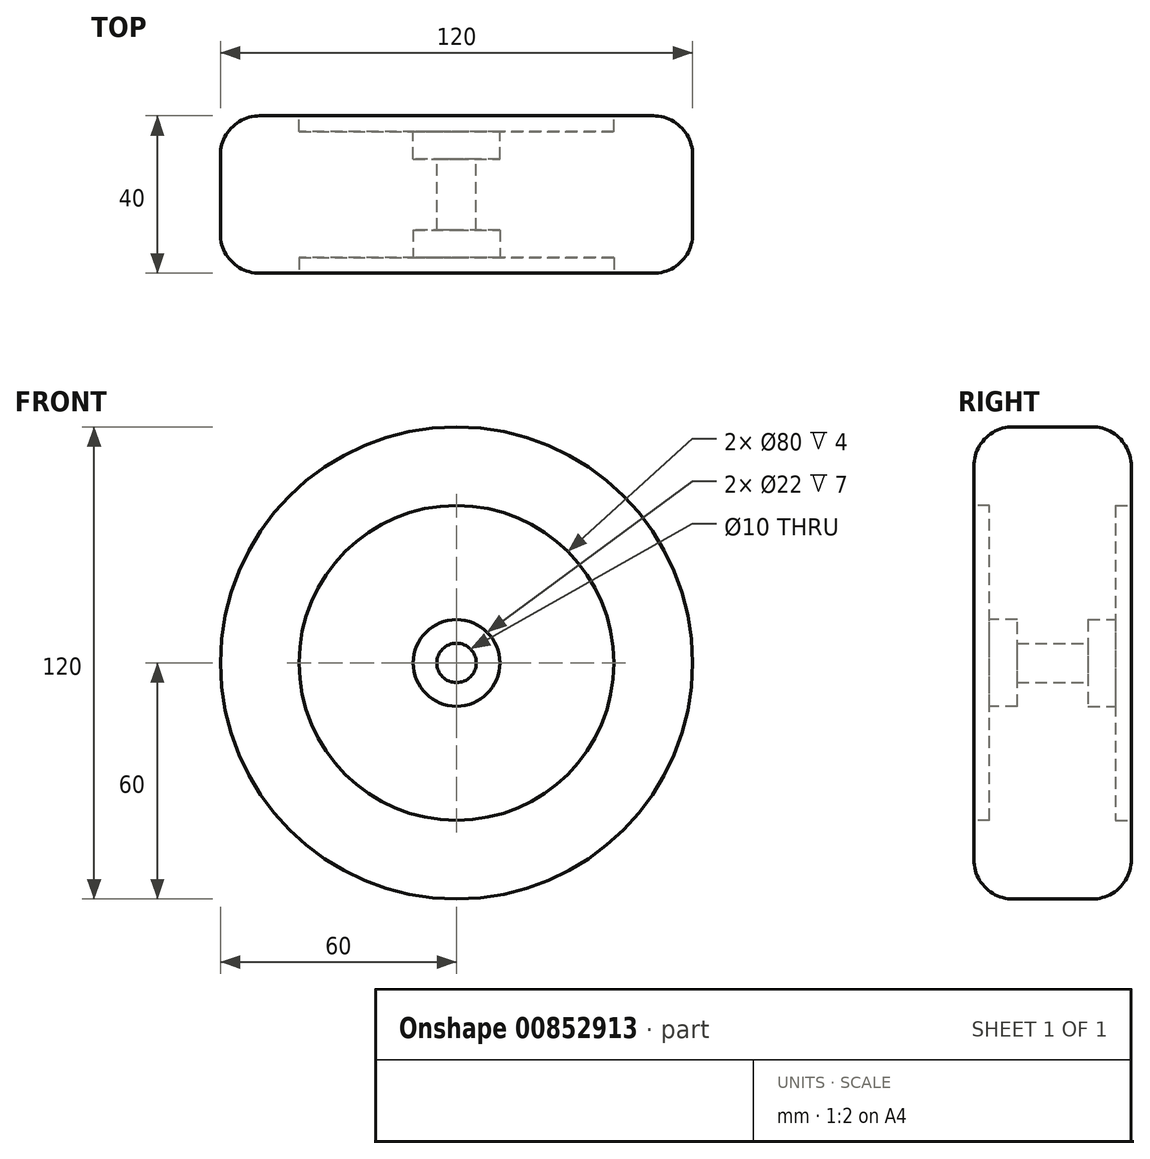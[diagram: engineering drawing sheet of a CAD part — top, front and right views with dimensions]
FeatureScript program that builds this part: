
annotation { "Feature Type Name" : "Feature", "Feature Type Description" : "" }
export const myFeature = defineFeature(function(context is Context, id is Id, definition is map)
    precondition{}
    {
        {
            var Q0;
            Q0=qCreatedBy(makeId("Front.planeOp"),FACE);
            var sketch = newSketch(context, id + "F0", { "sketchPlane" : qUnion([Q0])});
            skCircle(sketch, "E0", {"center": v(0, 0) * mm, "radius": 60 * mm});
            skSolve(sketch);
        }
        {
            var Q0;
            Q0=makeQuery(id+"F0.imprint","IMPRINT",FACE,{"disambiguationData":[TD([[makeQuery(id+"F0.imprint","IMPRINT",EDGE,{"derivedFrom":sQuery(id+"F0.wireOp",EDGE,"E0")}),1.0]])]});
            extrude(context, id + "F1", {"entities" : qUnion([Q0]), "depth" : 40 * mm, "offsetDistance" : 25 * mm});
        }
        {
            var Q0;
            Q0=makeQuery(id+"F1.opExtrude","CAP_FACE",FACE,{"disambiguationData":[OSD([sQuery(id+"F0.wireOp",EDGE,"E0")])],"isStart":false});
            var sketch = newSketch(context, id + "F2", { "sketchPlane" : qUnion([Q0])});
            skCircle(sketch, "E1", {"center": v(0, 0) * mm, "radius": 40 * mm});
            skSolve(sketch);
        }
        {
            var Q0;
            Q0=makeQuery(id+"F1.opExtrude","CAP_FACE",FACE,{"disambiguationData":[OSD([sQuery(id+"F0.wireOp",EDGE,"E0")])],"isStart":true});
            var Q1;
            Q1=makeQuery(id+"F1.opExtrude","SWEPT_FACE",FACE,{"disambiguationData":[OSD([sQuery(id+"F0.wireOp",EDGE,"E0")])]});
            fillet(context, id + "F3", {"entities" : qUnion([Q0, Q1]), "radius" : 10 * mm, "tangentPropagation" : true, "allowEdgeOverflow" : false});
        }
        {
            var Q0;
            Q0=makeQuery(id+"F2.imprint","IMPRINT",FACE,{"disambiguationData":[TD([[makeQuery(id+"F2.imprint","IMPRINT",EDGE,{"derivedFrom":sQuery(id+"F2.wireOp",EDGE,"E1")}),1.0]])]});
            extrude(context, id + "F4", {"entities" : qUnion([Q0]), "operationType" : NewBodyOperationType.REMOVE, "oppositeDirection" : true, "depth" : 4 * mm, "offsetDistance" : 25 * mm});
        }
        {
            var Q0;
            Q0=makeQuery(id+"F1.opExtrude","CAP_FACE",FACE,{"disambiguationData":[OSD([sQuery(id+"F0.wireOp",EDGE,"E0")])],"isStart":true});
            var sketch = newSketch(context, id + "F5", { "sketchPlane" : qUnion([Q0])});
            skCircle(sketch, "E2", {"center": v(0, 0) * mm, "radius": 40 * mm});
            skSolve(sketch);
        }
        {
            var Q0;
            Q0=makeQuery(id+"F5.imprint","IMPRINT",FACE,{"disambiguationData":[TD([[makeQuery(id+"F5.imprint","IMPRINT",EDGE,{"derivedFrom":sQuery(id+"F5.wireOp",EDGE,"E2")}),1.0]])]});
            extrude(context, id + "F6", {"entities" : qUnion([Q0]), "operationType" : NewBodyOperationType.REMOVE, "oppositeDirection" : true, "depth" : 4 * mm, "offsetDistance" : 25 * mm});
        }
        {
            var Q0;
            Q0=makeQuery(id+"F6.boolean.opBoolean","COPY",FACE,{"derivedFrom":makeQuery(id+"F6.opExtrude","CAP_FACE",FACE,{"disambiguationData":[OSD([sQuery(id+"F5.wireOp",EDGE,"E2")])],"isStart":false})});
            var sketch = newSketch(context, id + "F7", { "sketchPlane" : qUnion([Q0])});
            skCircle(sketch, "E3", {"center": v(0, 0) * mm, "radius": 11 * mm});
            skCircle(sketch, "E4", {"center": v(0, 0) * mm, "radius": 11.17 * mm});
            skSolve(sketch);
        }
        {
            var Q0;
            Q0=makeQuery(id+"F7.imprint","IMPRINT",FACE,{"disambiguationData":[TD([[makeQuery(id+"F7.imprint","IMPRINT",EDGE,{"derivedFrom":sQuery(id+"F7.wireOp",EDGE,"E3")}),1.0]])]});
            extrude(context, id + "F8", {"entities" : qUnion([Q0]), "operationType" : NewBodyOperationType.REMOVE, "oppositeDirection" : true, "depth" : 7 * mm, "offsetDistance" : 25 * mm});
        }
        {
            var Q0;
            Q0=makeQuery(id+"F4.boolean.opBoolean","COPY",FACE,{"derivedFrom":makeQuery(id+"F4.opExtrude","CAP_FACE",FACE,{"disambiguationData":[OSD([sQuery(id+"F2.wireOp",EDGE,"E1")])],"isStart":false})});
            var sketch = newSketch(context, id + "F9", { "sketchPlane" : qUnion([Q0])});
            skCircle(sketch, "E5", {"center": v(0, 0) * mm, "radius": 11 * mm});
            skSolve(sketch);
        }
        {
            var Q0;
            Q0=makeQuery(id+"F9.imprint","IMPRINT",FACE,{"disambiguationData":[TD([[makeQuery(id+"F9.imprint","IMPRINT",EDGE,{"derivedFrom":sQuery(id+"F9.wireOp",EDGE,"E5")}),1.0]])]});
            extrude(context, id + "F10", {"entities" : qUnion([Q0]), "operationType" : NewBodyOperationType.REMOVE, "oppositeDirection" : true, "depth" : 7 * mm, "offsetDistance" : 25 * mm});
        }
        {
            var Q0;
            Q0=makeQuery(id+"F6.boolean.opBoolean","COPY",FACE,{"derivedFrom":makeQuery(id+"F6.opExtrude","CAP_FACE",FACE,{"disambiguationData":[OSD([sQuery(id+"F5.wireOp",EDGE,"E2")])],"isStart":false})});
            var sketch = newSketch(context, id + "F11", { "sketchPlane" : qUnion([Q0])});
            skPoint(sketch, "E6", {"position": v(0, 0) * mm});
            skSolve(sketch);
        }
        {
            var Q0;
            Q0=sQuery(id+"F11.wireOp",VERTEX,"E6");
            var Q1;
            Q1=makeQuery(id+"F1.opExtrude","SWEPT_BODY",BODY,{"disambiguationData":[OSD([sQuery(id+"F0.wireOp",EDGE,"E0")])]});
            hole(context, id + "F12", {"style" : HoleStyle.SIMPLE, "endStyle" : HoleEndStyle.THROUGH, "holeDiameter" : 10 * mm, "majorDiameter" : 5 * mm, "isTappedThrough" : true, "tappedDepth" : 12 * mm, "tapClearance" : 3, "startFromSketch" : true, "locations" : qUnion([Q0]), "scope" : qUnion([Q1])});
        }
    });
